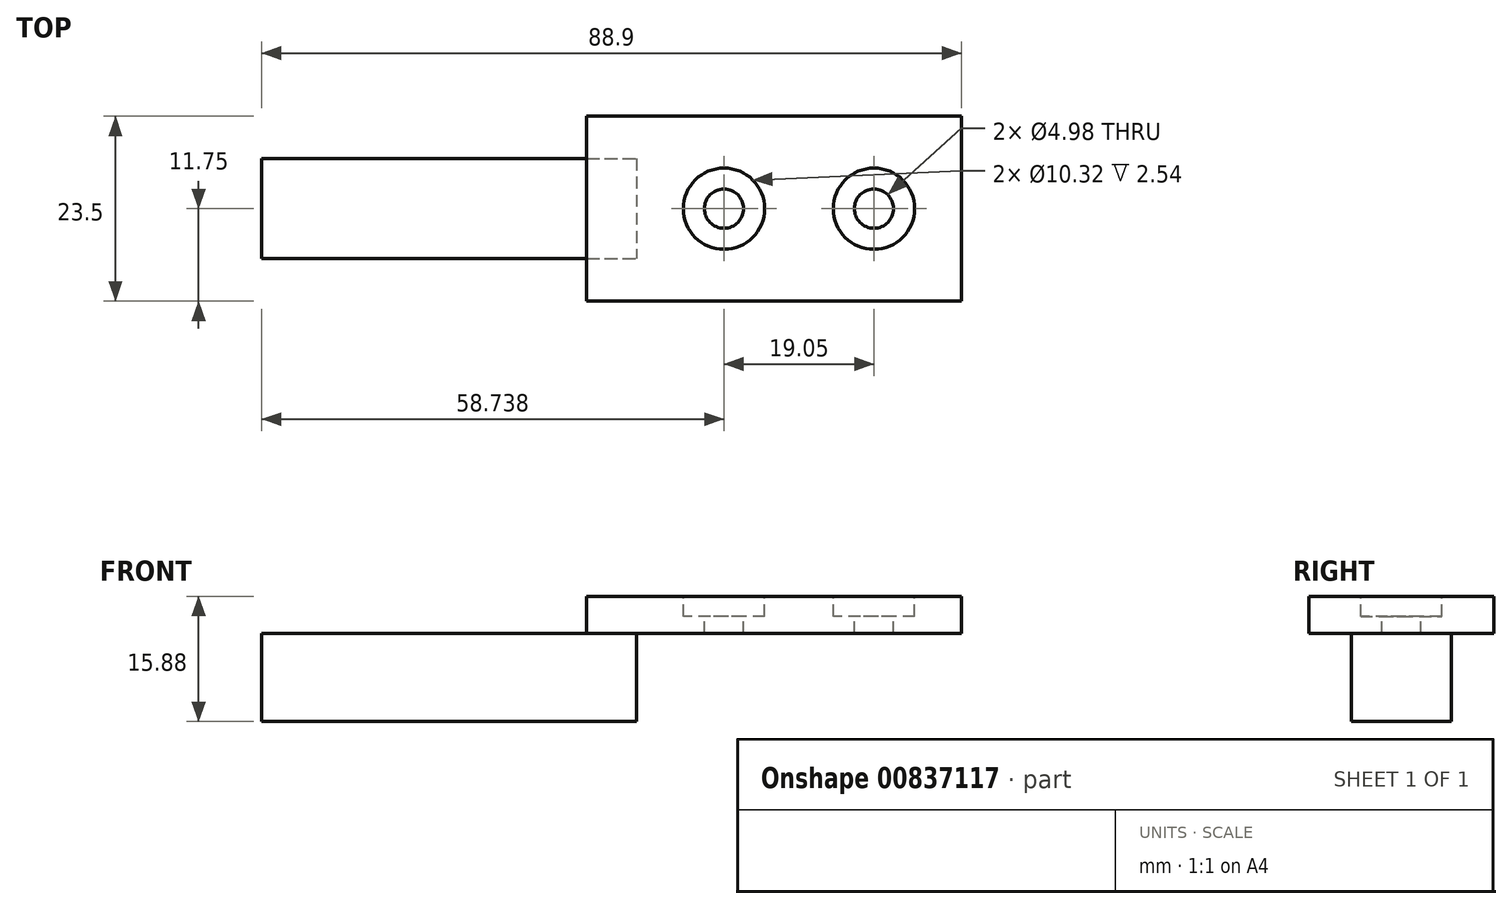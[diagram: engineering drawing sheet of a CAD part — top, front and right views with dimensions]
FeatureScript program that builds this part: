
annotation { "Feature Type Name" : "Feature", "Feature Type Description" : "" }
export const myFeature = defineFeature(function(context is Context, id is Id, definition is map)
    precondition{}
    {
        {
            var Q0;
            Q0=qCreatedBy(makeId("Top.planeOp"),FACE);
            var sketch = newSketch(context, id + "F0", { "sketchPlane" : qUnion([Q0])});
            skLineSegment(sketch, "E0.bottom", {"start": v(-44.45, 11.75) * mm, "end": v(44.45, 11.75) * mm});
            skLineSegment(sketch, "E0.top", {"start": v(-44.45, -11.75) * mm, "end": v(44.45, -11.75) * mm});
            skLineSegment(sketch, "E0.left", {"start": v(-44.45, 11.75) * mm, "end": v(-44.45, -11.75) * mm});
            skLineSegment(sketch, "E0.right", {"start": v(44.45, 11.75) * mm, "end": v(44.45, -11.75) * mm});
            skLineSegment(sketch, "E1", {"start": v(3.18, 11.75) * mm, "end": v(3.17, -11.75) * mm});
            skLineSegment(sketch, "E2", {"start": v(-44.45, 0) * mm, "end": v(44.45, 0) * mm, "construction": true});
            skCircle(sketch, "E3", {"center": v(33.34, 0) * mm, "radius": 5.16 * mm});
            skCircle(sketch, "E4", {"center": v(14.29, 0) * mm, "radius": 5.16 * mm});
            skCircle(sketch, "E5", {"center": v(14.29, 0) * mm, "radius": 2.49 * mm});
            skCircle(sketch, "E6", {"center": v(33.34, 0) * mm, "radius": 2.49 * mm});
            skLineSegment(sketch, "E7", {"start": v(-44.45, 6.35) * mm, "end": v(3.18, 6.35) * mm});
            skLineSegment(sketch, "E8", {"start": v(-44.45, -6.35) * mm, "end": v(3.18, -6.35) * mm});
            skLineSegment(sketch, "E9", {"start": v(-3.18, 11.75) * mm, "end": v(-3.18, -11.75) * mm});
            skSolve(sketch);
        }
        {
            var Q0;
            {var subQ0=sQuery(id+"F0.wireOp",EDGE,"E0.right");Q0=makeQuery(id+"F0.imprint","IMPRINT",FACE,{"disambiguationData":[TD([[makeQuery(id+"F0.imprint","IMPRINT",EDGE,{"derivedFrom":subQ0}),-1.0]])]});}
            var Q1;
            Q1=makeQuery(id+"F0.imprint","IMPRINT",FACE,{"disambiguationData":[TD([[makeQuery(id+"F0.imprint","IMPRINT",EDGE,{"derivedFrom":sQuery(id+"F0.wireOp",EDGE,"E4")}),1.0]])]});
            var Q2;
            Q2=makeQuery(id+"F0.imprint","IMPRINT",FACE,{"disambiguationData":[TD([[makeQuery(id+"F0.imprint","IMPRINT",EDGE,{"derivedFrom":sQuery(id+"F0.wireOp",EDGE,"E3")}),1.0]])]});
            var Q3;
            {var subQ0=sQuery(id+"F0.wireOp",EDGE,"E1");var subQ1=sQuery(id+"F0.wireOp",EDGE,"E0.bottom");var subQ2=makeQuery(id+"F0.imprint","INTERSECT",VERTEX,{"derivedFrom":[subQ1,subQ0]});Q3=makeQuery(id+"F0.imprint","IMPRINT",FACE,{"disambiguationData":[TD([[makeQuery(id+"F0.imprint","IMPRINT",EDGE,{"disambiguationData":[TD([[subQ2,1.0]])],"derivedFrom":subQ1}),-1.0]])]});}
            var Q4;
            {var subQ0=sQuery(id+"F0.wireOp",EDGE,"E7");var subQ1=sQuery(id+"F0.wireOp",EDGE,"E1");var subQ2=makeQuery(id+"F0.imprint","INTERSECT",VERTEX,{"derivedFrom":[subQ1,subQ0]});Q4=makeQuery(id+"F0.imprint","IMPRINT",FACE,{"disambiguationData":[TD([[makeQuery(id+"F0.imprint","IMPRINT",EDGE,{"disambiguationData":[TD([[subQ2,-1.0]])],"derivedFrom":subQ1}),-1.0]])]});}
            var Q5;
            {var subQ0=sQuery(id+"F0.wireOp",EDGE,"E1");var subQ1=sQuery(id+"F0.wireOp",EDGE,"E0.top");var subQ2=makeQuery(id+"F0.imprint","INTERSECT",VERTEX,{"derivedFrom":[subQ1,subQ0]});Q5=makeQuery(id+"F0.imprint","IMPRINT",FACE,{"disambiguationData":[TD([[makeQuery(id+"F0.imprint","IMPRINT",EDGE,{"disambiguationData":[TD([[subQ2,1.0]])],"derivedFrom":subQ1}),1.0]])]});}
            extrude(context, id + "F1", {"entities" : qUnion([Q0, Q1, Q2, Q3, Q4, Q5]), "oppositeDirection" : true, "depth" : 4.7 * mm, "offsetDistance" : 25.4 * mm});
        }
        {
            var Q0;
            {var subQ0=sQuery(id+"F0.wireOp",EDGE,"E7");Q0=makeQuery(id+"F0.imprint","IMPRINT",FACE,{"disambiguationData":[TD([[makeQuery(id+"F0.imprint","IMPRINT",EDGE,{"derivedFrom":subQ0}),-1.0]])]});}
            extrude(context, id + "F2", {"entities" : qUnion([Q0]), "operationType" : NewBodyOperationType.ADD, "oppositeDirection" : true, "depth" : 15.88 * mm, "offsetDistance" : 25.4 * mm});
        }
        {
            var Q0;
            Q0=makeQuery(id+"F0.imprint","IMPRINT",FACE,{"disambiguationData":[TD([[makeQuery(id+"F0.imprint","IMPRINT",EDGE,{"derivedFrom":sQuery(id+"F0.wireOp",EDGE,"E4")}),1.0]])]});
            var Q1;
            Q1=makeQuery(id+"F0.imprint","IMPRINT",FACE,{"disambiguationData":[TD([[makeQuery(id+"F0.imprint","IMPRINT",EDGE,{"derivedFrom":sQuery(id+"F0.wireOp",EDGE,"E3")}),1.0]])]});
            extrude(context, id + "F3", {"entities" : qUnion([Q0, Q1]), "operationType" : NewBodyOperationType.REMOVE, "oppositeDirection" : true, "depth" : 2.54 * mm, "offsetDistance" : 25.4 * mm});
        }
        {
            var Q0;
            {var subQ0=sQuery(id+"F0.wireOp",EDGE,"E7");var subQ1=sQuery(id+"F0.wireOp",EDGE,"E0.left");var subQ2=makeQuery(id+"F0.imprint","INTERSECT",VERTEX,{"derivedFrom":[subQ1,subQ0]});Q0=makeQuery(id+"F0.imprint","IMPRINT",FACE,{"disambiguationData":[TD([[makeQuery(id+"F0.imprint","IMPRINT",EDGE,{"disambiguationData":[TD([[subQ2,-1.0]])],"derivedFrom":subQ1}),1.0]])]});}
            extrude(context, id + "F4", {"entities" : qUnion([Q0]), "operationType" : NewBodyOperationType.REMOVE, "oppositeDirection" : true, "depth" : 4.7 * mm, "offsetDistance" : 25.4 * mm});
        }
    });
